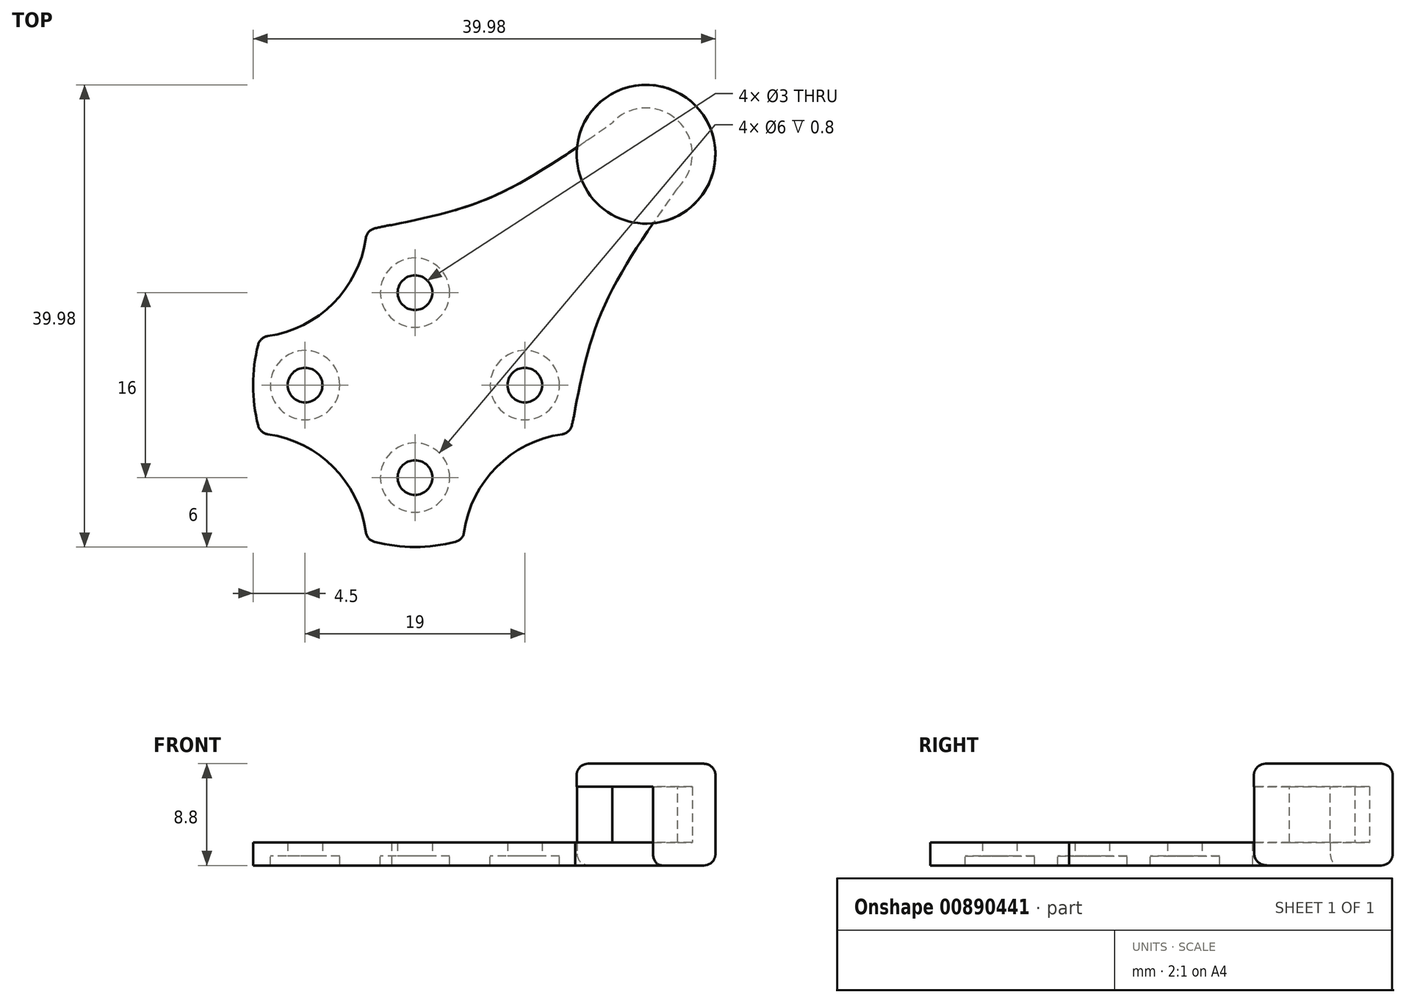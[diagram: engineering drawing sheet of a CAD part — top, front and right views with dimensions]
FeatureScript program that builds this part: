
annotation { "Feature Type Name" : "Feature", "Feature Type Description" : "" }
export const myFeature = defineFeature(function(context is Context, id is Id, definition is map)
    precondition{}
    {
        {
            var Q0;
            Q0=qCreatedBy(makeId("Top.planeOp"),FACE);
            var sketch = newSketch(context, id + "F0", { "sketchPlane" : qUnion([Q0])});
            skArc(sketch, "E0", {"start": v(-13.36, 4.17) * mm, "mid": v(-14, 0) * mm, "end": v(-13.36, -4.17) * mm});
            skCircle(sketch, "E1", {"center": v(19.98, 19.98) * mm, "radius": 4 * mm});
            skCircle(sketch, "E2", {"center": v(19.98, 19.98) * mm, "radius": 6 * mm});
            skCircle(sketch, "E3", {"center": v(9.5, 0) * mm, "radius": 1.5 * mm});
            skCircle(sketch, "E4", {"center": v(0, 8) * mm, "radius": 1.5 * mm});
            skCircle(sketch, "E5", {"center": v(-9.5, 0) * mm, "radius": 1.5 * mm});
            skCircle(sketch, "E6", {"center": v(0, -8) * mm, "radius": 1.5 * mm});
            skFitSpline(sketch, "E7", {"points": [v(17.05, 22.7) * mm, v(6.68, 16.3) * mm, v(-2.02, 13.85) * mm], "startDerivative": vector(-19.43, -13.68) * mm, "endDerivative": vector(-18.68, -3.78) * mm});
            skFitSpline(sketch, "E8.MirrorCS", {"points": [v(22.7, 17.05) * mm, v(16.3, 6.68) * mm, v(13.85, -2.02) * mm], "startDerivative": vector(-13.68, -19.43) * mm, "endDerivative": vector(-3.78, -18.68) * mm});
            skArc(sketch, "E9", {"start": v(-4.17, -13.36) * mm, "mid": v(-7.07, -7.07) * mm, "end": v(-13.36, -4.17) * mm});
            skArc(sketch, "E10", {"start": v(-13.36, 4.17) * mm, "mid": v(-7.07, 7.07) * mm, "end": v(-4.17, 13.36) * mm});
            skArc(sketch, "E11", {"start": v(13.36, -4.17) * mm, "mid": v(7.07, -7.07) * mm, "end": v(4.17, -13.36) * mm});
            skArc(sketch, "E12.trimOffspring", {"start": v(-4.17, -13.36) * mm, "mid": v(0, -14) * mm, "end": v(4.17, -13.36) * mm});
            skArc(sketch, "E13.trimOffspring", {"start": v(13.36, -4.17) * mm, "mid": v(13.65, -3.1) * mm, "end": v(13.85, -2.02) * mm});
            skArc(sketch, "E14.trimOffspring", {"start": v(-2.02, 13.85) * mm, "mid": v(-3.1, 13.65) * mm, "end": v(-4.17, 13.36) * mm});
            skCircle(sketch, "E15", {"center": v(-9.5, 0) * mm, "radius": 3 * mm});
            skCircle(sketch, "E16", {"center": v(0, 8) * mm, "radius": 3 * mm});
            skCircle(sketch, "E17", {"center": v(9.5, 0) * mm, "radius": 3 * mm});
            skCircle(sketch, "E18", {"center": v(0, -8) * mm, "radius": 3 * mm});
            skSolve(sketch);
        }
        {
            var Q0;
            Q0 = qSketchRegion(id + "F0", true);
            var Q1;
            {var subQ0=sQuery(id+"F0.wireOp",EDGE,"E1");var subQ1=makeQuery(id+"F0.imprint","INTERSECT",VERTEX,{"derivedFrom":[subQ0,sQuery(id+"F0.wireOp",EDGE,"E7")]});Q1=makeQuery(id+"F0.imprint","IMPRINT",FACE,{"disambiguationData":[TD([[makeQuery(id+"F0.imprint","IMPRINT",EDGE,{"disambiguationData":[TD([[subQ1,-1.0]])],"derivedFrom":subQ0}),1.0]])]});}
            var Q2;
            Q2=makeQuery(id+"F0.imprint","IMPRINT",FACE,{"disambiguationData":[TD([[makeQuery(id+"F0.imprint","IMPRINT",EDGE,{"derivedFrom":sQuery(id+"F0.wireOp",EDGE,"E3")}),-1.0]])]});
            var Q3;
            Q3=makeQuery(id+"F0.imprint","IMPRINT",FACE,{"disambiguationData":[TD([[makeQuery(id+"F0.imprint","IMPRINT",EDGE,{"derivedFrom":sQuery(id+"F0.wireOp",EDGE,"E4")}),-1.0]])]});
            var Q4;
            Q4=makeQuery(id+"F0.imprint","IMPRINT",FACE,{"disambiguationData":[TD([[makeQuery(id+"F0.imprint","IMPRINT",EDGE,{"derivedFrom":sQuery(id+"F0.wireOp",EDGE,"E5")}),-1.0]])]});
            var Q5;
            Q5=makeQuery(id+"F0.imprint","IMPRINT",FACE,{"disambiguationData":[TD([[makeQuery(id+"F0.imprint","IMPRINT",EDGE,{"derivedFrom":sQuery(id+"F0.wireOp",EDGE,"E6")}),-1.0]])]});
            extrude(context, id + "F1", {"entities" : qUnion([Q0, Q1, Q2, Q3, Q4, Q5]), "depth" : 1.2 * mm, "offsetDistance" : 25 * mm});
        }
        {
            var Q0;
            {var subQ0=sQuery(id+"F0.wireOp",EDGE,"E7");var subQ1=sQuery(id+"F0.wireOp",EDGE,"E1");var subQ2=makeQuery(id+"F0.imprint","INTERSECT",VERTEX,{"derivedFrom":[subQ1,subQ0]});Q0=makeQuery(id+"F0.imprint","IMPRINT",FACE,{"disambiguationData":[TD([[makeQuery(id+"F0.imprint","IMPRINT",EDGE,{"disambiguationData":[TD([[subQ2,1.0]])],"derivedFrom":subQ1}),-1.0]])]});}
            var Q1;
            {var subQ0=sQuery(id+"F0.wireOp",EDGE,"E1");var subQ1=makeQuery(id+"F0.imprint","INTERSECT",VERTEX,{"derivedFrom":[subQ0,sQuery(id+"F0.wireOp",EDGE,"E7")]});Q1=makeQuery(id+"F0.imprint","IMPRINT",FACE,{"disambiguationData":[TD([[makeQuery(id+"F0.imprint","IMPRINT",EDGE,{"disambiguationData":[TD([[subQ1,-1.0]])],"derivedFrom":subQ0}),1.0]])]});}
            var Q2;
            {var subQ0=sQuery(id+"F0.wireOp",EDGE,"E7");var subQ1=sQuery(id+"F0.wireOp",EDGE,"E1");var subQ2=makeQuery(id+"F0.imprint","INTERSECT",VERTEX,{"derivedFrom":[subQ1,subQ0]});Q2=makeQuery(id+"F0.imprint","IMPRINT",FACE,{"disambiguationData":[TD([[makeQuery(id+"F0.imprint","IMPRINT",EDGE,{"disambiguationData":[TD([[subQ2,-1.0]])],"derivedFrom":subQ1}),-1.0]])]});}
            extrude(context, id + "F2", {"entities" : qUnion([Q0, Q1, Q2]), "operationType" : NewBodyOperationType.ADD, "depth" : 8 * mm, "offsetDistance" : 25 * mm});
        }
        {
            var Q0;
            {var subQ0=sQuery(id+"F0.wireOp",EDGE,"E1");var subQ1=makeQuery(id+"F0.imprint","INTERSECT",VERTEX,{"derivedFrom":[subQ0,sQuery(id+"F0.wireOp",EDGE,"E7")]});Q0=makeQuery(id+"F0.imprint","IMPRINT",FACE,{"disambiguationData":[TD([[makeQuery(id+"F0.imprint","IMPRINT",EDGE,{"disambiguationData":[TD([[subQ1,-1.0]])],"derivedFrom":subQ0}),1.0]])]});}
            var Q1;
            {var subQ0=sQuery(id+"F0.wireOp",EDGE,"E7");var subQ1=sQuery(id+"F0.wireOp",EDGE,"E1");var subQ2=makeQuery(id+"F0.imprint","INTERSECT",VERTEX,{"derivedFrom":[subQ1,subQ0]});Q1=makeQuery(id+"F0.imprint","IMPRINT",FACE,{"disambiguationData":[TD([[makeQuery(id+"F0.imprint","IMPRINT",EDGE,{"disambiguationData":[TD([[subQ2,-1.0]])],"derivedFrom":subQ1}),-1.0]])]});}
            extrude(context, id + "F3", {"entities" : qUnion([Q0, Q1]), "operationType" : NewBodyOperationType.REMOVE, "oppositeDirection" : true, "depth" : -6 * mm, "offsetDistance" : 25 * mm});
        }
        {
            var Q0;
            {var subQ0=sQuery(id+"F0.wireOp",EDGE,"E1");var subQ1=makeQuery(id+"F0.imprint","INTERSECT",VERTEX,{"derivedFrom":[subQ0,sQuery(id+"F0.wireOp",EDGE,"E7")]});Q0=makeQuery(id+"F0.imprint","IMPRINT",FACE,{"disambiguationData":[TD([[makeQuery(id+"F0.imprint","IMPRINT",EDGE,{"disambiguationData":[TD([[subQ1,-1.0]])],"derivedFrom":subQ0}),1.0]])]});}
            var Q1;
            {var subQ0=sQuery(id+"F0.wireOp",EDGE,"E7");var subQ1=sQuery(id+"F0.wireOp",EDGE,"E1");var subQ2=makeQuery(id+"F0.imprint","INTERSECT",VERTEX,{"derivedFrom":[subQ1,subQ0]});Q1=makeQuery(id+"F0.imprint","IMPRINT",FACE,{"disambiguationData":[TD([[makeQuery(id+"F0.imprint","IMPRINT",EDGE,{"disambiguationData":[TD([[subQ2,-1.0]])],"derivedFrom":subQ1}),-1.0]])]});}
            extrude(context, id + "F4", {"entities" : qUnion([Q0, Q1]), "depth" : 1.2 * mm, "offsetDistance" : 25 * mm});
        }
        {
            var Q0;
            {var subQ0=sQuery(id+"F0.wireOp",EDGE,"E7");var subQ1=sQuery(id+"F0.wireOp",EDGE,"E1");var subQ2=makeQuery(id+"F0.imprint","INTERSECT",VERTEX,{"derivedFrom":[subQ1,subQ0]});Q0=makeQuery(id+"F0.imprint","IMPRINT",FACE,{"disambiguationData":[TD([[makeQuery(id+"F0.imprint","IMPRINT",EDGE,{"disambiguationData":[TD([[subQ2,1.0]])],"derivedFrom":subQ1}),-1.0]])]});}
            var Q1;
            {var subQ0=sQuery(id+"F0.wireOp",EDGE,"E1");var subQ1=makeQuery(id+"F0.imprint","INTERSECT",VERTEX,{"derivedFrom":[subQ0,sQuery(id+"F0.wireOp",EDGE,"E7")]});Q1=makeQuery(id+"F0.imprint","IMPRINT",FACE,{"disambiguationData":[TD([[makeQuery(id+"F0.imprint","IMPRINT",EDGE,{"disambiguationData":[TD([[subQ1,-1.0]])],"derivedFrom":subQ0}),1.0]])]});}
            var Q2;
            {var subQ0=sQuery(id+"F0.wireOp",EDGE,"E7");var subQ1=sQuery(id+"F0.wireOp",EDGE,"E1");var subQ2=makeQuery(id+"F0.imprint","INTERSECT",VERTEX,{"derivedFrom":[subQ1,subQ0]});Q2=makeQuery(id+"F0.imprint","IMPRINT",FACE,{"disambiguationData":[TD([[makeQuery(id+"F0.imprint","IMPRINT",EDGE,{"disambiguationData":[TD([[subQ2,-1.0]])],"derivedFrom":subQ1}),-1.0]])]});}
            extrude(context, id + "F5", {"entities" : qUnion([Q0, Q1, Q2]), "depth" : -1 * mm, "offsetDistance" : 25 * mm});
        }
        {
            var Q0;
            Q0=makeQuery(id+"F5.opExtrude","SWEPT_BODY",BODY,{"disambiguationData":[OSD([sQuery(id+"F0.wireOp",EDGE,"E2")])]});
            deleteBodies(context, id + "F6", {"entities" : qUnion([Q0])});
        }
        {
            var Q0;
            Q0=makeQuery(id+"F0.imprint","IMPRINT",FACE,{"disambiguationData":[TD([[makeQuery(id+"F0.imprint","IMPRINT",EDGE,{"derivedFrom":sQuery(id+"F0.wireOp",EDGE,"E0")}),1.0]])]});
            var Q1;
            {var subQ0=sQuery(id+"F0.wireOp",EDGE,"E7");var subQ1=sQuery(id+"F0.wireOp",EDGE,"E1");var subQ2=makeQuery(id+"F0.imprint","INTERSECT",VERTEX,{"derivedFrom":[subQ1,subQ0]});Q1=makeQuery(id+"F0.imprint","IMPRINT",FACE,{"disambiguationData":[TD([[makeQuery(id+"F0.imprint","IMPRINT",EDGE,{"disambiguationData":[TD([[subQ2,-1.0]])],"derivedFrom":subQ1}),-1.0]])]});}
            var Q2;
            {var subQ0=sQuery(id+"F0.wireOp",EDGE,"E1");var subQ1=makeQuery(id+"F0.imprint","INTERSECT",VERTEX,{"derivedFrom":[subQ0,sQuery(id+"F0.wireOp",EDGE,"E7")]});Q2=makeQuery(id+"F0.imprint","IMPRINT",FACE,{"disambiguationData":[TD([[makeQuery(id+"F0.imprint","IMPRINT",EDGE,{"disambiguationData":[TD([[subQ1,-1.0]])],"derivedFrom":subQ0}),1.0]])]});}
            var Q3;
            {var subQ0=sQuery(id+"F0.wireOp",EDGE,"E7");var subQ1=sQuery(id+"F0.wireOp",EDGE,"E1");var subQ2=makeQuery(id+"F0.imprint","INTERSECT",VERTEX,{"derivedFrom":[subQ1,subQ0]});Q3=makeQuery(id+"F0.imprint","IMPRINT",FACE,{"disambiguationData":[TD([[makeQuery(id+"F0.imprint","IMPRINT",EDGE,{"disambiguationData":[TD([[subQ2,1.0]])],"derivedFrom":subQ1}),-1.0]])]});}
            extrude(context, id + "F7", {"entities" : qUnion([Q0, Q1, Q2, Q3]), "depth" : -0.8 * mm, "offsetDistance" : 25 * mm});
        }
        {
            var Q0;
            Q0=makeQuery(id+"F3.boolean.opBoolean","SPLIT",BODY,{"disambiguationData":[OD(0.0)],"derivedFrom":makeQuery(id+"F1.opExtrude","SWEPT_BODY",BODY,{"disambiguationData":[OSD([sQuery(id+"F0.wireOp",EDGE,"E0"),sQuery(id+"F0.wireOp",EDGE,"E2"),sQuery(id+"F0.wireOp",EDGE,"E3"),sQuery(id+"F0.wireOp",EDGE,"E4"),sQuery(id+"F0.wireOp",EDGE,"E5"),sQuery(id+"F0.wireOp",EDGE,"E6"),sQuery(id+"F0.wireOp",EDGE,"E7"),sQuery(id+"F0.wireOp",EDGE,"E8.MirrorCS"),sQuery(id+"F0.wireOp",EDGE,"E9"),sQuery(id+"F0.wireOp",EDGE,"E10"),sQuery(id+"F0.wireOp",EDGE,"E11"),sQuery(id+"F0.wireOp",EDGE,"E12.trimOffspring"),sQuery(id+"F0.wireOp",EDGE,"E13.trimOffspring"),sQuery(id+"F0.wireOp",EDGE,"E14.trimOffspring")])]})});
            var Q1;
            Q1=makeQuery(id+"F3.boolean.opBoolean","SPLIT",BODY,{"disambiguationData":[OD(1.0)],"derivedFrom":makeQuery(id+"F1.opExtrude","SWEPT_BODY",BODY,{"disambiguationData":[OSD([sQuery(id+"F0.wireOp",EDGE,"E0"),sQuery(id+"F0.wireOp",EDGE,"E2"),sQuery(id+"F0.wireOp",EDGE,"E3"),sQuery(id+"F0.wireOp",EDGE,"E4"),sQuery(id+"F0.wireOp",EDGE,"E5"),sQuery(id+"F0.wireOp",EDGE,"E6"),sQuery(id+"F0.wireOp",EDGE,"E7"),sQuery(id+"F0.wireOp",EDGE,"E8.MirrorCS"),sQuery(id+"F0.wireOp",EDGE,"E9"),sQuery(id+"F0.wireOp",EDGE,"E10"),sQuery(id+"F0.wireOp",EDGE,"E11"),sQuery(id+"F0.wireOp",EDGE,"E12.trimOffspring"),sQuery(id+"F0.wireOp",EDGE,"E13.trimOffspring"),sQuery(id+"F0.wireOp",EDGE,"E14.trimOffspring")])]})});
            var Q2;
            Q2=makeQuery(id+"F4.opExtrude","SWEPT_BODY",BODY,{"disambiguationData":[OSD([sQuery(id+"F0.wireOp",EDGE,"E1"),sQuery(id+"F0.wireOp",EDGE,"E2"),sQuery(id+"F0.wireOp",EDGE,"E7"),sQuery(id+"F0.wireOp",EDGE,"E8.MirrorCS")])]});
            var Q3;
            Q3=makeQuery(id+"F7.opExtrude","SWEPT_BODY",BODY,{"disambiguationData":[OSD([sQuery(id+"F0.wireOp",EDGE,"E0"),sQuery(id+"F0.wireOp",EDGE,"E2"),sQuery(id+"F0.wireOp",EDGE,"E7"),sQuery(id+"F0.wireOp",EDGE,"E8.MirrorCS"),sQuery(id+"F0.wireOp",EDGE,"E9"),sQuery(id+"F0.wireOp",EDGE,"E10"),sQuery(id+"F0.wireOp",EDGE,"E11"),sQuery(id+"F0.wireOp",EDGE,"E12.trimOffspring"),sQuery(id+"F0.wireOp",EDGE,"E13.trimOffspring"),sQuery(id+"F0.wireOp",EDGE,"E14.trimOffspring"),sQuery(id+"F0.wireOp",EDGE,"E15"),sQuery(id+"F0.wireOp",EDGE,"E16"),sQuery(id+"F0.wireOp",EDGE,"E17"),sQuery(id+"F0.wireOp",EDGE,"E18")])]});
            booleanBodies(context, id + "F8", {"operationType" : BooleanOperationType.UNION, "tools" : qUnion([Q0, Q1, Q2, Q3])});
        }
        {
            var Q0;
            {var subQ0=sQuery(id+"F0.wireOp",EDGE,"E12.trimOffspring");var subQ1=sQuery(id+"F0.wireOp",EDGE,"E11");Q0=makeQuery(id+"F8.opBoolean","MERGE",EDGE,{"derivedFrom":[makeQuery(id+"F1.opExtrude","SWEPT_EDGE",EDGE,{"disambiguationData":[OSD([subQ1,subQ0])]}),makeQuery(id+"F7.opExtrude","SWEPT_EDGE",EDGE,{"disambiguationData":[OSD([subQ1,subQ0])]})]});}
            var Q1;
            {var subQ0=sQuery(id+"F0.wireOp",EDGE,"E12.trimOffspring");var subQ1=sQuery(id+"F0.wireOp",EDGE,"E9");Q1=makeQuery(id+"F8.opBoolean","MERGE",EDGE,{"derivedFrom":[makeQuery(id+"F1.opExtrude","SWEPT_EDGE",EDGE,{"disambiguationData":[OSD([subQ1,subQ0])]}),makeQuery(id+"F7.opExtrude","SWEPT_EDGE",EDGE,{"disambiguationData":[OSD([subQ1,subQ0])]})]});}
            var Q2;
            {var subQ0=sQuery(id+"F0.wireOp",EDGE,"E13.trimOffspring");var subQ1=sQuery(id+"F0.wireOp",EDGE,"E11");Q2=makeQuery(id+"F8.opBoolean","MERGE",EDGE,{"derivedFrom":[makeQuery(id+"F1.opExtrude","SWEPT_EDGE",EDGE,{"disambiguationData":[OSD([subQ1,subQ0])]}),makeQuery(id+"F7.opExtrude","SWEPT_EDGE",EDGE,{"disambiguationData":[OSD([subQ1,subQ0])]})]});}
            var Q3;
            {var subQ0=sQuery(id+"F0.wireOp",EDGE,"E9");var subQ1=sQuery(id+"F0.wireOp",EDGE,"E0");Q3=makeQuery(id+"F8.opBoolean","MERGE",EDGE,{"derivedFrom":[makeQuery(id+"F1.opExtrude","SWEPT_EDGE",EDGE,{"disambiguationData":[OSD([subQ1,subQ0])]}),makeQuery(id+"F7.opExtrude","SWEPT_EDGE",EDGE,{"disambiguationData":[OSD([subQ1,subQ0])]})]});}
            var Q4;
            {var subQ0=sQuery(id+"F0.wireOp",EDGE,"E10");var subQ1=sQuery(id+"F0.wireOp",EDGE,"E0");Q4=makeQuery(id+"F8.opBoolean","MERGE",EDGE,{"derivedFrom":[makeQuery(id+"F1.opExtrude","SWEPT_EDGE",EDGE,{"disambiguationData":[OSD([subQ1,subQ0])]}),makeQuery(id+"F7.opExtrude","SWEPT_EDGE",EDGE,{"disambiguationData":[OSD([subQ1,subQ0])]})]});}
            var Q5;
            {var subQ0=sQuery(id+"F0.wireOp",EDGE,"E14.trimOffspring");var subQ1=sQuery(id+"F0.wireOp",EDGE,"E10");Q5=makeQuery(id+"F8.opBoolean","MERGE",EDGE,{"derivedFrom":[makeQuery(id+"F1.opExtrude","SWEPT_EDGE",EDGE,{"disambiguationData":[OSD([subQ1,subQ0])]}),makeQuery(id+"F7.opExtrude","SWEPT_EDGE",EDGE,{"disambiguationData":[OSD([subQ1,subQ0])]})]});}
            var Q6;
            Q6=makeQuery(id+"F2.opExtrude","CAP_EDGE",EDGE,{"disambiguationData":[OSD([sQuery(id+"F0.wireOp",EDGE,"E2")])],"isStart":false});
            var Q7;
            Q7=makeQuery(id+"F7.opExtrude","CAP_EDGE",EDGE,{"disambiguationData":[OSD([sQuery(id+"F0.wireOp",EDGE,"E2")])],"isStart":false});
            fillet(context, id + "F9", {"entities" : qUnion([Q0, Q1, Q2, Q3, Q4, Q5, Q6, Q7]), "radius" : 1 * mm, "tangentPropagation" : true, "allowEdgeOverflow" : false});
        }
    });
